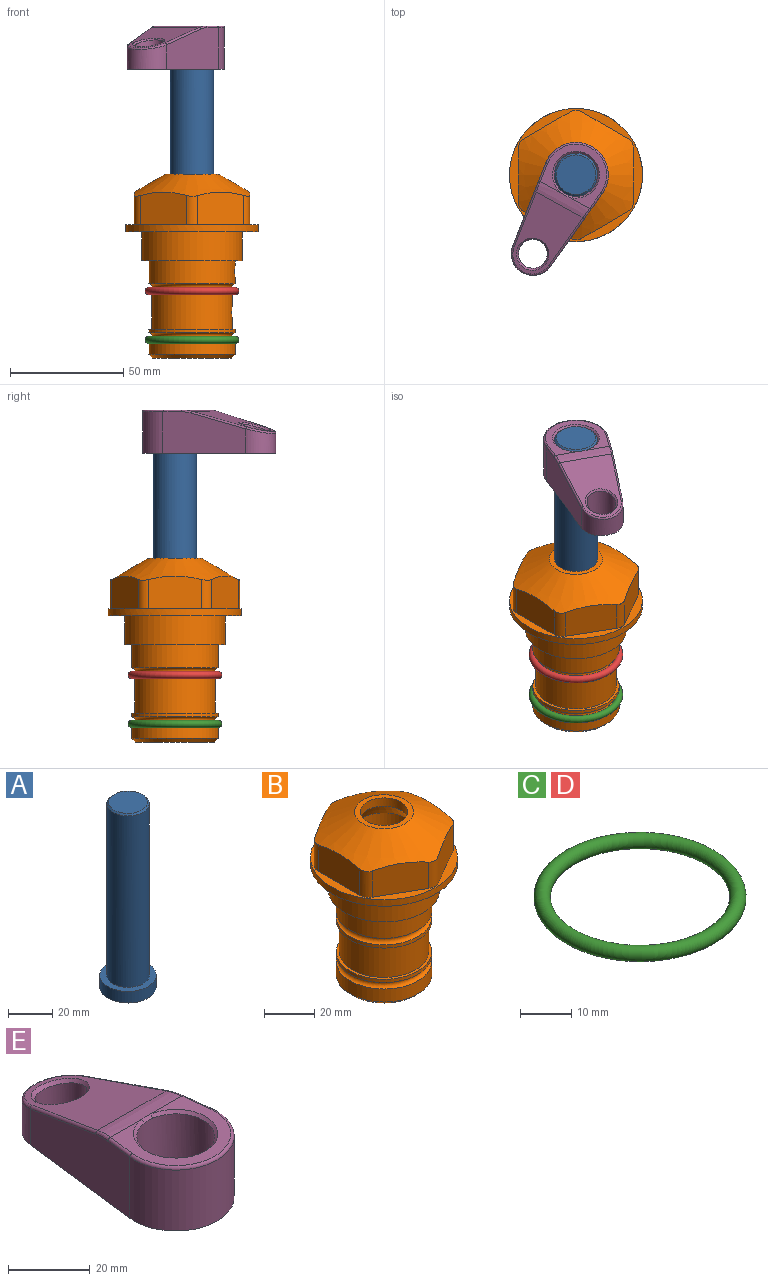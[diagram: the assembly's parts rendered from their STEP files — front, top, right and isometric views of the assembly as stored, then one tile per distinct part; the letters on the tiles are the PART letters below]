
ASSEMBLY  parts=5 mates=4
PART A: 6 faces, bbox 25.4x25.4x101.6 mm
  f0: plane 17.46x17.46mm, normal (0,0,1), area 239.5mm2, adj f5
  f1: plane 25.4x25.4mm, normal (0,0,-1), area 506.7mm2, adj f2
  f2: cylinder r=12.7mm len=25.4mm, axis (0,0,1), area 506.7mm2, adj f1,f3
  f3: plane 25.4x25.4mm, normal (0,0,1), area 221.7mm2, adj f2,f4
  f4: cylinder r=9.53mm len=94.46mm, axis (0,0,1), area 5653mm2, adj f3,f5
  f5: cone r=8.73mm half-angle=45deg, axis (0,0,-1), area 64.4mm2, adj f0,f4
PART B: 36 faces, bbox 58.7x58.7x81 mm
  f0: cylinder r=17.78mm len=35.56mm, axis (0,0,1), area 1670.8mm2, adj f23,f24,f31
  f1: cylinder r=19.05mm len=38.1mm, axis (0,0,1), area 1191.9mm2, adj f26,f27,f30
  f2: plane 58.66x58.66mm, normal (0,0,-1), area 1150.6mm2, adj f3,f28
  f3: cylinder r=29.33mm len=58.66mm, axis (0,0,-1), area 585.1mm2, adj f2,f4
  f4: plane 58.66x58.66mm, normal (0,0,1), area 475.9mm2, adj f3,f5,f6,f7,f8,f9,f10,f11
  f5: plane 20.32x14.34mm, normal (-0.5,0.87,0), area 324.4mm2, adj f4,f15,f16,f17
  f6: plane 20.32x14.34mm, normal (0.5,0.87,0), area 324.4mm2, adj f4,f14,f15,f17
  f7: plane 23.48x14.34mm, normal (1,0,0), area 324.4mm2, adj f4,f13,f14,f17
  f8: plane 20.32x14.34mm, normal (0.5,-0.87,0), area 324.4mm2, adj f4,f12,f13,f17
  f9: plane 20.32x14.34mm, normal (-0.5,-0.87,0), area 324.4mm2, adj f4,f11,f12,f17
  f10: plane 23.48x14.34mm, normal (-1,0,0), area 324.4mm2, adj f4,f11,f16,f17
  f11: cylinder r=5.08mm len=12.85mm, axis (0,0,-1), area 67.2mm2, adj f4,f9,f10,f17
  f12: cylinder r=5.08mm len=12.85mm, axis (0,0,-1), area 67.2mm2, adj f4,f8,f9,f17
  f13: cylinder r=5.08mm len=12.85mm, axis (0,0,-1), area 67.2mm2, adj f4,f7,f8,f17
  f14: cylinder r=5.08mm len=12.85mm, axis (0,0,-1), area 67.2mm2, adj f4,f6,f7,f17
  f15: cylinder r=5.08mm len=12.85mm, axis (0,0,-1), area 67.2mm2, adj f4,f5,f6,f17
  f16: cylinder r=5.08mm len=12.85mm, axis (0,0,-1), area 67.2mm2, adj f4,f5,f10,f17
  f17: cone r=11.73mm half-angle=60deg, axis (0,0,-1), area 2071.8mm2, adj f5,f6,f7,f8,f9,f10,f11,f12
  f18: plane 23.46x23.46mm, normal (0,0,1), area 147.4mm2, adj f17,f35
  f19: plane 34.93x34.93mm, normal (0,0,-1), area 958mm2, adj f29
  f20: cylinder r=19.05mm len=38.1mm, axis (0,0,1), area 760.1mm2, adj f21,f29
  f21: torus R=19.05mm, axis (0,0,1), area 565.3mm2, adj f20,f22
  f22: cylinder r=19.05mm len=38.1mm, axis (0,0,1), area 190mm2, adj f21,f23
  f23: plane 38.1x38.1mm, normal (0,0,1), area 146.9mm2, adj f0,f22
  f24: plane 38.1x38.1mm, normal (0,0,-1), area 146.9mm2, adj f0,f25
  f25: cylinder r=19.05mm len=38.1mm, axis (0,0,1), area 190mm2, adj f24,f26
  f26: torus R=19.05mm, axis (0,0,1), area 565.3mm2, adj f1,f25
  f27: plane 44.45x44.45mm, normal (0,0,-1), area 411.7mm2, adj f1,f28
  f28: cylinder r=22.23mm len=44.45mm, axis (0,0,1), area 1773.5mm2, adj f2,f27
  f29: cone r=19.05mm half-angle=45deg, axis (0,0,1), area 257.5mm2, adj f19,f20
  f30: cylinder r=3.17mm len=6.75mm, axis (-1,0,0), area 128mm2, adj f1,f33
  f31: cylinder r=3.17mm len=6.35mm, axis (-1,0,0), area 102.5mm2, adj f0,f33
  f32: plane 25.4x25.4mm, normal (0,0,1), area 506.7mm2, adj f33
  f33: cylinder r=12.7mm len=66.42mm, axis (0,0,-1), area 5236.2mm2, adj f30,f31,f32,f34
  f34: cone r=9.53mm half-angle=30deg, axis (0,0,-1), area 443.4mm2, adj f33,f35
  f35: cylinder r=9.53mm len=19.05mm, axis (0,0,-1), area 240.9mm2, adj f18,f34
PART C: 1 faces, bbox 44.7x44.7x3.2 mm
  f0: torus R=19.05mm, axis (0,0,1), area 1193.9mm2
PART D: same geometry as C
PART E: 31 faces, bbox 31.7x65.5x19.8 mm
  f0: plane 39.12x18.26mm, normal (0.99,0.12,0), area 612.2mm2, adj f1,f4,f7,f11,f13,f15
  f1: cylinder r=9.53mm len=18.91mm, axis (0,0,-1), area 296.1mm2, adj f0,f2,f7,f17
  f2: plane 39.12x18.26mm, normal (-0.99,0.12,0), area 612.2mm2, adj f1,f4,f7,f12,f14,f16
  f3: cylinder r=6.35mm len=12.7mm, axis (0,0,-1), area 362.4mm2, adj f7,f18
  f4: cylinder r=14.29mm len=28.58mm, axis (0,0,-1), area 882.2mm2, adj f0,f2,f7,f10
  f5: cylinder r=9.53mm len=19.05mm, axis (0,0,-1), area 1092.6mm2, adj f7,f19,f20
  f6: plane 26.99x23.69mm, normal (0,0,1), area 216.2mm2, adj f9,f10,f11,f12,f19
  f7: plane 63.5x28.58mm, normal (0,0,-1), area 661.8mm2, adj f0,f1,f2,f3,f4,f5,f22,f23
  f8: plane 33.52x23.6mm, normal (0,0.26,0.97), area 486mm2, adj f9,f15,f16,f17,f18
  f9: cylinder r=19.05mm len=24.72mm, axis (1,0,0), area 120.4mm2, adj f6,f8,f13,f14,f20
  f10: torus R=13.49mm, axis (0,0,1), area 59mm2, adj f4,f6,f11,f12
  f11: cylinder r=0.79mm len=8.67mm, axis (0.12,-0.99,0), area 10.8mm2, adj f0,f6,f10,f13
  f12: cylinder r=0.79mm len=8.67mm, axis (0.12,0.99,0), area 10.8mm2, adj f2,f6,f10,f14
  f13: bspline ~4.95x1.42mm, area 6.1mm2, adj f0,f9,f11,f15
  f14: bspline ~4.95x1.42mm, area 6.1mm2, adj f2,f9,f12,f16
  f15: cylinder r=0.79mm len=25.95mm, axis (0.12,-0.96,0.26), area 32.9mm2, adj f0,f8,f13,f17
  f16: cylinder r=0.79mm len=25.95mm, axis (0.12,0.96,-0.26), area 32.9mm2, adj f2,f8,f14,f17
  f17: bspline ~18.91x8.38mm, area 30mm2, adj f1,f8,f15,f16
  f18: bspline ~14.29x14.29mm, area 48.3mm2, adj f3,f8
  f19: cone r=9.53mm half-angle=45deg, axis (0,0,1), area 66.5mm2, adj f5,f6,f20
  f20: bspline ~3.22x0.96mm, area 3.5mm2, adj f5,f9,f19
  f21: plane 2.75x2.72mm, normal (0,0,-1), area 2.9mm2, adj f23,f25,f28
  f22: plane 23.05x15.88mm, normal (-0.99,-0.12,0), area 323.6mm2, adj f7,f25,f26,f27,f28,f29
  f23: plane 23.05x15.88mm, normal (0.99,-0.12,0), area 323.6mm2, adj f7,f21,f25,f27,f28,f30
  f24: cylinder r=9.53mm len=10.69mm, axis (0,0,-1), area 114.7mm2, adj f7,f27,f29,f30
  f25: cylinder r=12.7mm len=20.59mm, axis (0,0,-1), area 381.1mm2, adj f7,f21,f22,f23,f26,f28
  f26: plane 2.75x2.72mm, normal (0,0,-1), area 2.9mm2, adj f22,f25,f28
  f27: plane 19.72x18.37mm, normal (0,-0.26,-0.97), area 291.8mm2, adj f22,f23,f24,f28,f29,f30
  f28: cylinder r=15.88mm len=19.92mm, axis (1,0,0), area 54.8mm2, adj f21,f22,f23,f25,f26,f27
  f29: cylinder r=1.59mm len=11mm, axis (0,0,-1), area 34.7mm2, adj f7,f22,f24,f27
  f30: cylinder r=1.59mm len=11mm, axis (0,0,-1), area 34.7mm2, adj f7,f23,f24,f27
PLACE A rot(axis=(0,0,1),151.4deg) t=(0,0,27.24)mm
PLACE B at identity fixed
PLACE C t=(0,0,-23.18)mm
PLACE D t=(0,0,-1.59)mm
PLACE E rot(axis=(0,0,1),151.4deg) t=(0,0,27.24)mm
MATE fastened B.f0 <-> C.f0  axis (0,0,1) through (0,0,-47.69)mm
MATE cylindrical A.f2 <-> B.f0  axis (0,0,-1) through (0,0,-10.86)mm
MATE fastened E.f4 <-> A.f2  axis (0,0,1) through (0,0,90.74)mm
MATE fastened B.f0 <-> D.f0  axis (0,0,1) through (0,0,-26.1)mm
